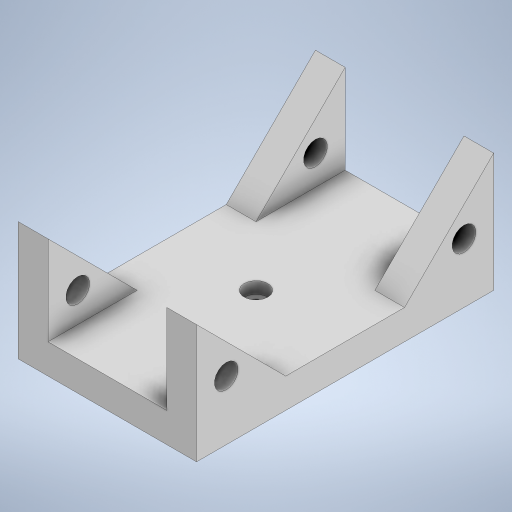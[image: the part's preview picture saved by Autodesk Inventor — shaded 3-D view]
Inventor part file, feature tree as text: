
AUTODESK INVENTOR PART (.ipt)
format: ipt  version: 2024 (Build 280153000, 153)  size: 263,680 bytes
history: native  units: mm
features: extrude x4, mirror x1, sketch x1
ambient origin geometry x8: Origin, YZ Plane, XZ Plane, XY Plane, X Axis, Y Axis, Z Axis, Center Point
bodies: Solid1 (feature_tree)
feature tree (6):
  extrude  "Extrusion1"  TaperAngle=45.0deg  [1 undecoded]
  extrude  "Extrusion2"  Depth=5.0mm
  mirror  "Mirror1"
  extrude  "Extrusion3"  Depth=2.0mm
  extrude  "Extrusion4"  Depth=2.0mm
  sketch  "Sketch2"  dims[d0=50.0mm d1=45.0deg d2=5.0mm d4=40.0mm d5=4.0mm d6=20.0mm d7=5.0mm d8=15.0mm d9=5.0mm d10=0.0mm d11=10.0mm d12=0.0mm d13=4.0mm d14=2.0mm d15=0.0mm d16=2.0mm d17=0.0mm d18=0.0mm]
note: 1 required parameter value undecoded (feature->parameter linkage not recoverable at this tier; creation-order binding heuristic only, values carry confidence <= 0.55)
